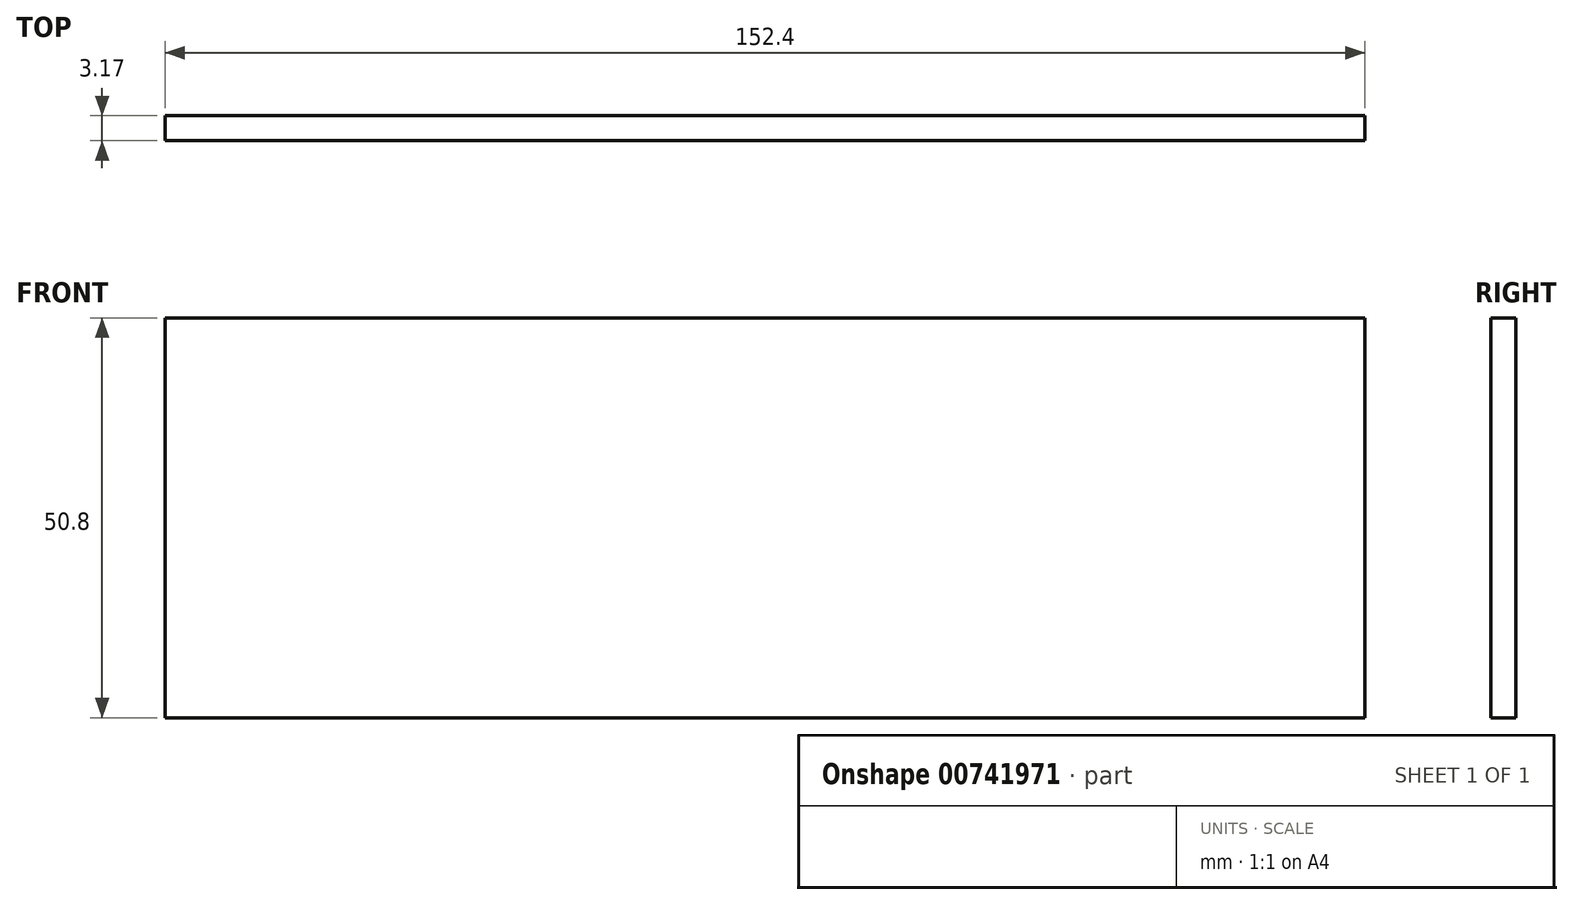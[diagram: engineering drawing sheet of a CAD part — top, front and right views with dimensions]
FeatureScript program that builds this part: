
annotation { "Feature Type Name" : "Feature", "Feature Type Description" : "" }
export const myFeature = defineFeature(function(context is Context, id is Id, definition is map)
    precondition{}
    {
        {
            var Q0;
            Q0=qCreatedBy(makeId("Front.planeOp"),FACE);
            var sketch = newSketch(context, id + "F0", { "sketchPlane" : qUnion([Q0])});
            skLineSegment(sketch, "E0.bottom", {"start": v(-83.73, -1.44) * mm, "end": v(68.67, -1.44) * mm});
            skLineSegment(sketch, "E0.top", {"start": v(-83.73, -52.24) * mm, "end": v(68.67, -52.24) * mm});
            skLineSegment(sketch, "E0.left", {"start": v(-83.73, -1.44) * mm, "end": v(-83.73, -52.24) * mm});
            skLineSegment(sketch, "E0.right", {"start": v(68.67, -1.44) * mm, "end": v(68.67, -52.24) * mm});
            skSolve(sketch);
        }
        {
            var Q0;
            Q0 = qSketchRegion(id + "F0", true);
            extrude(context, id + "F1", {"entities" : qUnion([Q0]), "depth" : 3.17 * mm, "offsetDistance" : 25.4 * mm});
        }
    });
